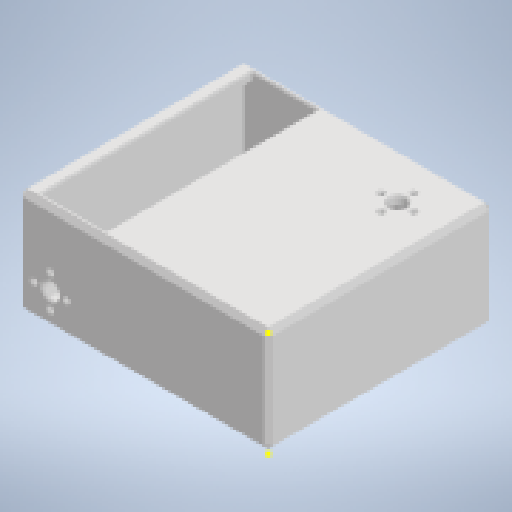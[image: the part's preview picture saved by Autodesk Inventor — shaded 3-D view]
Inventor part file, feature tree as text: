
AUTODESK INVENTOR PART (.ipt)
format: ipt  version: 2023 (Build 270158000, 158)  size: 332,800 bytes
history: native  units: mm
features: sketch x23, extrude x10, chamfer x5
ambient origin geometry x8: Origin, YZ Plane, XZ Plane, XY Plane, X Axis, Y Axis, Z Axis, Center Point
bodies: Solid1 (feature_tree)
feature tree (38):
  extrude  "Extrusion1"  Depth=155.0mm
  extrude  "Extrusion2"  Depth=5.0mm
  extrude  "Extrusion3"  Depth=5.0mm
  extrude  "Extrusion4"  Depth=55.0mm TaperAngle=0.0deg
  extrude  "Extrusion5"  Depth=10.0mm
  extrude  "Extrusion6"  Depth=30.0mm
  extrude  "Extrusion7"  Depth=5.0mm
  sketch  "Sketch8"  dims[d18=20.0mm]
  sketch  "Sketch9"  dims[d19=10.0mm d20=20.0mm d21=0.0mm]
  sketch  "Sketch10"  dims[d22=10.0mm]
  chamfer  "Chamfer1"  Distance=20.0mm
  chamfer  "Chamfer3"  Distance=5.0mm
  extrude  "Extrusion9"  Depth=40.0mm TaperAngle=360.0deg
  sketch  "Sketch13"  dims[d24=5.0mm]
  extrude  "Extrusion10"  Depth=10.0mm
  chamfer  "Chamfer4"  Distance=2.0mm Angle=45.0deg
  chamfer  "Chamfer5"  Distance=2.0mm Angle=45.0deg
  sketch  "Sketch15"  dims[d28=3.0mm d29=40.0mm d31=360.0deg]
  sketch  "Sketch16"  dims[d33=5.0mm d34=0.0mm d35=10.0mm d44=1.0mm d45=2.0mm d46=45.0deg d50=1.0mm d51=2.0mm d52=45.0deg]
  sketch  "Sketch17"  dims[d53=30.0mm d54=30.0mm d55=5.0mm d56=0.0mm]
  sketch  "Sketch18"  dims[d57=20.0mm d58=0.0mm]
  sketch  "Sketch19"  dims[d59=1.0mm d60=2.0mm d61=45.0deg]
  sketch  "Sketch20"  dims[d62=3.0mm d63=2.0mm d64=45.0deg]
  sketch  "Sketch21"  dims[d66=3.0mm]
  sketch  "Sketch22"  dims[d67=10.0mm]
  sketch  "Sketch23"  dims[d68=40.0mm d70=360.0deg]
  extrude  "Extrusion11"  Depth=30.0mm
  chamfer  "Chamfer6"  Distance=5.0mm
  sketch  "Sketch24"  dims[d72=10.0mm d73=0.0mm d74=1.0mm d75=2.0mm d76=45.0deg d30=0.872665mm d32=0.872665mm]
  sketch  "Sketch1"  dims[d0=130.0mm d1=155.0mm]
  sketch  "Sketch2"  dims[d2=60.0mm d3=0.0mm d4=5.0mm]
  sketch  "Sketch3"  dims[d5=5.0mm d6=5.0mm]
  sketch  "Sketch4"  dims[d7=5.0mm d8=55.0mm d9=0.0mm]
  sketch  "Sketch5"  dims[d10=5.0mm d11=0.0mm d12=10.0mm]
  sketch  "Sketch6"  dims[d13=30.0mm d14=30.0mm]
  sketch  "Sketch7"  dims[d15=5.0mm d16=0.0mm d17=20.0mm]
  sketch  "Sketch12"  dims[d23=5.0mm]
  sketch  "Sketch14"  dims[d25=40.0mm d26=5.0mm d27=0.0mm]
